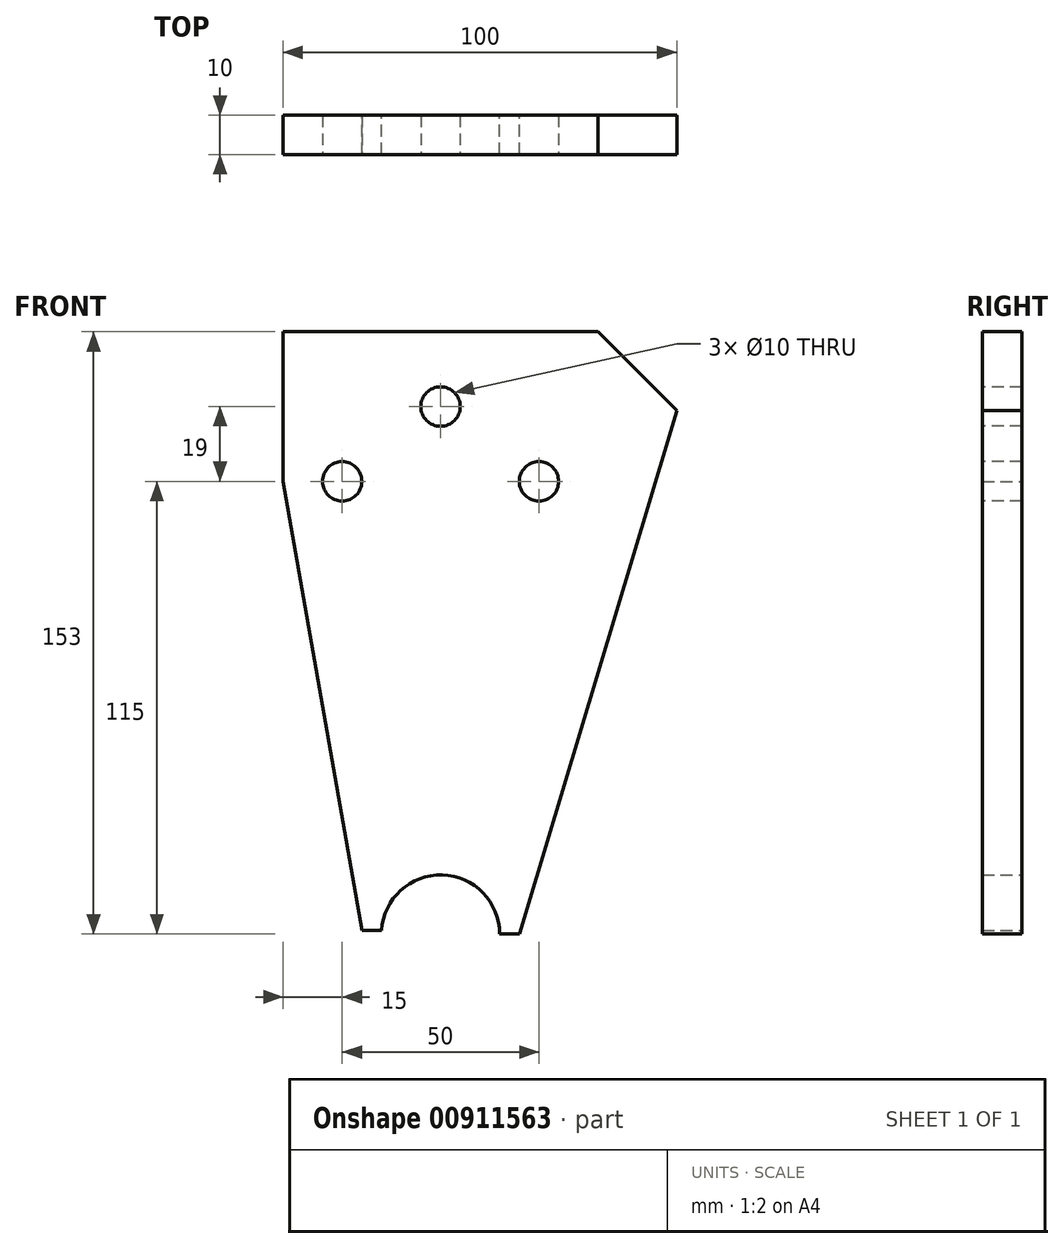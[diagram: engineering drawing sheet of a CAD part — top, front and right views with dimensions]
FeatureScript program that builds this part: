
annotation { "Feature Type Name" : "Feature", "Feature Type Description" : "" }
export const myFeature = defineFeature(function(context is Context, id is Id, definition is map)
    precondition{}
    {
        {
            var Q0;
            Q0=qCreatedBy(makeId("Front.planeOp"),FACE);
            var sketch = newSketch(context, id + "F0", { "sketchPlane" : qUnion([Q0])});
            skLineSegment(sketch, "E0", {"start": v(-61.9, 38) * mm, "end": v(18.1, 38) * mm});
            skLineSegment(sketch, "E1", {"start": v(-61.9, 38) * mm, "end": v(-61.9, 0) * mm});
            skLineSegment(sketch, "E2", {"start": v(18.1, 38) * mm, "end": v(38.1, 18) * mm});
            skArc(sketch, "E3", {"start": v(-6.9, -115) * mm, "mid": v(-21.45, -100) * mm, "end": v(-36.87, -114.1) * mm});
            skLineSegment(sketch, "E4", {"start": v(-6.9, -115) * mm, "end": v(-1.9, -115) * mm});
            skLineSegment(sketch, "E5", {"start": v(-36.87, -114.1) * mm, "end": v(-41.87, -114.1) * mm});
            skLineSegment(sketch, "E6", {"start": v(-61.9, 0) * mm, "end": v(-41.87, -114.1) * mm});
            skLineSegment(sketch, "E7", {"start": v(38.1, 18) * mm, "end": v(-1.9, -115) * mm});
            skSolve(sketch);
        }
        {
            var Q0;
            Q0=makeQuery(id+"F0.imprint","IMPRINT",FACE,{"disambiguationData":[TD([[makeQuery(id+"F0.imprint","IMPRINT",EDGE,{"derivedFrom":sQuery(id+"F0.wireOp",EDGE,"E0")}),-1.0]])]});
            extrude(context, id + "F1", {"entities" : qUnion([Q0]), "depth" : 10 * mm, "offsetDistance" : 25 * mm});
        }
        {
            var Q0;
            Q0=makeQuery(id+"F1.opExtrude","CAP_FACE",FACE,{"disambiguationData":[OSD([sQuery(id+"F0.wireOp",EDGE,"E0"),sQuery(id+"F0.wireOp",EDGE,"E1"),sQuery(id+"F0.wireOp",EDGE,"E2"),sQuery(id+"F0.wireOp",EDGE,"E3"),sQuery(id+"F0.wireOp",EDGE,"E4"),sQuery(id+"F0.wireOp",EDGE,"E5"),sQuery(id+"F0.wireOp",EDGE,"E6"),sQuery(id+"F0.wireOp",EDGE,"E7")])],"isStart":false});
            var sketch = newSketch(context, id + "F2", { "sketchPlane" : qUnion([Q0])});
            skCircle(sketch, "E8", {"center": v(-21.9, 19) * mm, "radius": 5 * mm});
            skCircle(sketch, "E9", {"center": v(-46.9, 0) * mm, "radius": 5 * mm});
            skCircle(sketch, "E10", {"center": v(3.1, 0) * mm, "radius": 5 * mm});
            skSolve(sketch);
        }
        {
            var Q0;
            Q0=sQuery(id+"F2.wireOp",VERTEX,"E9.center");
            var Q1;
            Q1=sQuery(id+"F2.wireOp",VERTEX,"E8.center");
            var Q2;
            Q2=sQuery(id+"F2.wireOp",VERTEX,"E10.center");
            var Q3;
            Q3=makeQuery(id+"F1.opExtrude","SWEPT_BODY",BODY,{"disambiguationData":[OSD([sQuery(id+"F0.wireOp",EDGE,"E0"),sQuery(id+"F0.wireOp",EDGE,"E1"),sQuery(id+"F0.wireOp",EDGE,"E2"),sQuery(id+"F0.wireOp",EDGE,"E3"),sQuery(id+"F0.wireOp",EDGE,"E4"),sQuery(id+"F0.wireOp",EDGE,"E5"),sQuery(id+"F0.wireOp",EDGE,"E6"),sQuery(id+"F0.wireOp",EDGE,"E7")])]});
            hole(context, id + "F3", {"style" : HoleStyle.SIMPLE, "endStyle" : HoleEndStyle.THROUGH, "holeDiameter" : 10 * mm, "majorDiameter" : 5 * mm, "isTappedThrough" : true, "tappedDepth" : 12 * mm, "tapClearance" : 3, "locations" : qUnion([Q0, Q1, Q2]), "scope" : qUnion([Q3])});
        }
    });
